# Revit family: 63__LF_UN_Emilux_Turijn I_R17
name_source: partatom
category: Lighting Fixtures
revit_build: Autodesk Revit 2017 (Build: 20190508_0315(x64)
units: mm (PartAtom-declared; Revit-internal decimal feet)

## family parameters
Always vertical = Yes
Cut with Voids When Loaded = Yes
Light Source = Yes
Part Type = Normal
Room Calculation Point = No
Round Connector Dimension = Use Diameter
Shared = No
Work Plane-Based = No

## types (2) — shared parameters
Apparent Load = 36 VA
Article Number = 1TI12036840
Assembly Code = 63.0
Color Filter = 16777215
Description = Turijn I LED 4050lm 4000K Ra80 (36W)
Dimming Lamp Color Temperature Shift = <None>
Emit from Line Length = 1153 mm
IfcExportAs = IfcLightFixtureType
IfcExportType = POINTSOURCE
Lamp = LED
Manufacturer = EMILUX
Model = Turijn
Tilt Angle = 90.00°
Type Comments = Turijn 1195mm
URL = https://www.emilux.nl
Wattage Comments = 36W

## per-type parameters (varying)
| type | Cost | LED Driver | Photometric Web File |
| LED 4050lm 4000K Ra80 (36W) | 0 $ | Yes | Emilux TURIJN 30X120 36W 4050Lm 4000K Ra80_LDT.ies |
| LED 4000lm 3000K Ra80 (36W) | 150 $ | No | Emilux TURIJN 30X120 36W 4000Lm 3000K Ra80_LDT.ies |

## geometry (parser evidence)
native form markers: Sweep x7
no freeform markers — native parametric forms only
